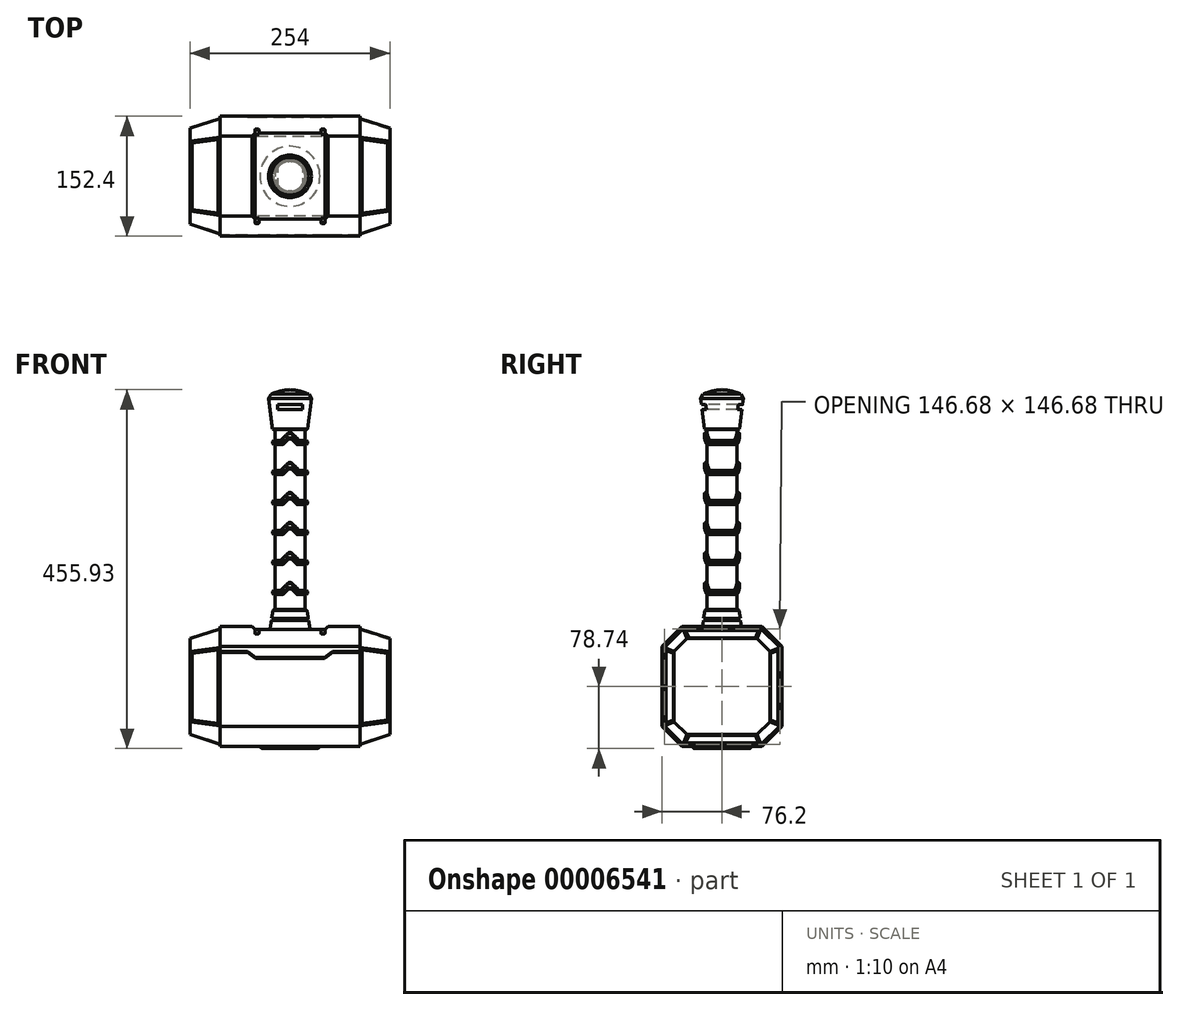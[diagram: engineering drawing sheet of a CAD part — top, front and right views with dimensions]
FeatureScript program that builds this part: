
annotation { "Feature Type Name" : "Feature", "Feature Type Description" : "" }
export const myFeature = defineFeature(function(context is Context, id is Id, definition is map)
    precondition{}
    {
        {
            var Q0;
            Q0=qCreatedBy(makeId("Top.planeOp"),FACE);
            var sketch = newSketch(context, id + "F0", { "sketchPlane" : qUnion([Q0])});
            skLineSegment(sketch, "E0.bottom", {"start": v(-88.9, -76.2) * mm, "end": v(88.9, -76.2) * mm});
            skLineSegment(sketch, "E0.top", {"start": v(-88.9, 76.2) * mm, "end": v(88.9, 76.2) * mm});
            skLineSegment(sketch, "E0.left", {"start": v(-88.9, -76.2) * mm, "end": v(-88.9, 76.2) * mm});
            skLineSegment(sketch, "E0.right", {"start": v(88.9, -76.2) * mm, "end": v(88.9, 76.2) * mm});
            skSolve(sketch);
        }
        {
            var Q0;
            Q0=makeQuery(id+"F0.imprint","IMPRINT",FACE,{"disambiguationData":[TD([[makeQuery(id+"F0.imprint","IMPRINT",EDGE,{"derivedFrom":sQuery(id+"F0.wireOp",EDGE,"E0.bottom")}),1.0]])]});
            extrude(context, id + "F1", {"entities" : qUnion([Q0]), "depth" : 152.4 * mm});
        }
        {
            var Q0;
            Q0=makeQuery(id+"F1.opExtrude","CAP_EDGE",EDGE,{"disambiguationData":[OSD([sQuery(id+"F0.wireOp",EDGE,"E0.bottom")])],"isStart":false});
            var Q1;
            Q1=makeQuery(id+"F1.opExtrude","CAP_EDGE",EDGE,{"disambiguationData":[OSD([sQuery(id+"F0.wireOp",EDGE,"E0.top")])],"isStart":false});
            var Q2;
            Q2=makeQuery(id+"F1.opExtrude","CAP_EDGE",EDGE,{"disambiguationData":[OSD([sQuery(id+"F0.wireOp",EDGE,"E0.bottom")])],"isStart":true});
            var Q3;
            Q3=makeQuery(id+"F1.opExtrude","CAP_EDGE",EDGE,{"disambiguationData":[OSD([sQuery(id+"F0.wireOp",EDGE,"E0.top")])],"isStart":true});
            chamfer(context, id + "F2", {"entities" : qUnion([Q0, Q1, Q2, Q3]), "width" : 25.4 * mm, "tangentPropagation" : true});
        }
        {
            var Q0;
            Q0=makeQuery(id+"F1.opExtrude","SWEPT_FACE",FACE,{"disambiguationData":[OSD([sQuery(id+"F0.wireOp",EDGE,"E0.left")])]});
            var sketch = newSketch(context, id + "F3", { "sketchPlane" : qUnion([Q0])});
            skLineSegment(sketch, "E1.0", {"start": v(-49.75, 149.86) * mm, "end": v(-73.66, 125.95) * mm});
            skLineSegment(sketch, "E1.1", {"start": v(49.75, 149.86) * mm, "end": v(-49.75, 149.86) * mm});
            skLineSegment(sketch, "E1.2", {"start": v(73.66, 125.95) * mm, "end": v(49.75, 149.86) * mm});
            skLineSegment(sketch, "E1.3", {"start": v(73.66, 26.45) * mm, "end": v(73.66, 125.95) * mm});
            skLineSegment(sketch, "E1.4", {"start": v(49.75, 2.54) * mm, "end": v(73.66, 26.45) * mm});
            skLineSegment(sketch, "E1.5", {"start": v(-73.66, 125.95) * mm, "end": v(-73.66, 26.45) * mm});
            skLineSegment(sketch, "E1.6", {"start": v(-49.75, 2.54) * mm, "end": v(49.75, 2.54) * mm});
            skLineSegment(sketch, "E1.7", {"start": v(-73.66, 26.45) * mm, "end": v(-49.75, 2.54) * mm});
            skSolve(sketch);
        }
        {
            var Q0;
            Q0=makeQuery(id+"F3.imprint","IMPRINT",FACE,{"disambiguationData":[TD([[makeQuery(id+"F3.imprint","IMPRINT",EDGE,{"derivedFrom":sQuery(id+"F3.wireOp",EDGE,"E1.0")}),1.0]])]});
            extrude(context, id + "F4", {"entities" : qUnion([Q0]), "operationType" : NewBodyOperationType.ADD, "depth" : 38.1 * mm});
        }
        {
            var Q0;
            Q0=makeQuery(id+"F4.opExtrude","CAP_FACE",FACE,{"disambiguationData":[OSD([sQuery(id+"F3.wireOp",EDGE,"E1.0"),sQuery(id+"F3.wireOp",EDGE,"E1.1"),sQuery(id+"F3.wireOp",EDGE,"E1.2"),sQuery(id+"F3.wireOp",EDGE,"E1.3"),sQuery(id+"F3.wireOp",EDGE,"E1.4"),sQuery(id+"F3.wireOp",EDGE,"E1.5"),sQuery(id+"F3.wireOp",EDGE,"E1.6"),sQuery(id+"F3.wireOp",EDGE,"E1.7")])],"isStart":false});
            chamfer(context, id + "F5", {"entities" : qUnion([Q0]), "chamferType" : ChamferType.OFFSET_ANGLE, "width" : 12.7 * mm, "oppositeDirection" : false, "angle" : 72 * degree, "tangentPropagation" : true});
        }
        {
            var Q0;
            Q0=makeQuery(id+"F1.opExtrude","SWEPT_FACE",FACE,{"disambiguationData":[OSD([sQuery(id+"F0.wireOp",EDGE,"E0.right")])]});
            var sketch = newSketch(context, id + "F6", { "sketchPlane" : qUnion([Q0])});
            skLineSegment(sketch, "E2.0", {"start": v(-73.66, 26.45) * mm, "end": v(-49.75, 2.54) * mm});
            skLineSegment(sketch, "E2.1", {"start": v(-73.66, 125.95) * mm, "end": v(-73.66, 26.45) * mm});
            skLineSegment(sketch, "E2.2", {"start": v(-49.75, 149.86) * mm, "end": v(-73.66, 125.95) * mm});
            skLineSegment(sketch, "E2.3", {"start": v(49.75, 149.86) * mm, "end": v(-49.75, 149.86) * mm});
            skLineSegment(sketch, "E2.4", {"start": v(73.66, 125.95) * mm, "end": v(49.75, 149.86) * mm});
            skLineSegment(sketch, "E2.5", {"start": v(-49.75, 2.54) * mm, "end": v(49.75, 2.54) * mm});
            skLineSegment(sketch, "E2.6", {"start": v(73.66, 26.45) * mm, "end": v(73.66, 125.95) * mm});
            skLineSegment(sketch, "E2.7", {"start": v(49.75, 2.54) * mm, "end": v(73.66, 26.45) * mm});
            skSolve(sketch);
        }
        {
            var Q0;
            Q0=makeQuery(id+"F6.imprint","IMPRINT",FACE,{"disambiguationData":[TD([[makeQuery(id+"F6.imprint","IMPRINT",EDGE,{"derivedFrom":sQuery(id+"F6.wireOp",EDGE,"E2.0")}),1.0]])]});
            extrude(context, id + "F7", {"entities" : qUnion([Q0]), "operationType" : NewBodyOperationType.ADD, "depth" : 38.1 * mm});
        }
        {
            var Q0;
            Q0=makeQuery(id+"F7.opExtrude","CAP_FACE",FACE,{"disambiguationData":[OSD([sQuery(id+"F6.wireOp",EDGE,"E2.0"),sQuery(id+"F6.wireOp",EDGE,"E2.1"),sQuery(id+"F6.wireOp",EDGE,"E2.2"),sQuery(id+"F6.wireOp",EDGE,"E2.3"),sQuery(id+"F6.wireOp",EDGE,"E2.4"),sQuery(id+"F6.wireOp",EDGE,"E2.5"),sQuery(id+"F6.wireOp",EDGE,"E2.6"),sQuery(id+"F6.wireOp",EDGE,"E2.7")])],"isStart":false});
            chamfer(context, id + "F8", {"entities" : qUnion([Q0]), "chamferType" : ChamferType.OFFSET_ANGLE, "width" : 12.7 * mm, "oppositeDirection" : false, "angle" : 72 * degree, "tangentPropagation" : true});
        }
        {
            var Q0;
            Q0=makeQuery(id+"F1.opExtrude","CAP_FACE",FACE,{"disambiguationData":[OSD([sQuery(id+"F0.wireOp",EDGE,"E0.bottom"),sQuery(id+"F0.wireOp",EDGE,"E0.top"),sQuery(id+"F0.wireOp",EDGE,"E0.left"),sQuery(id+"F0.wireOp",EDGE,"E0.right")])],"isStart":true});
            var sketch = newSketch(context, id + "F9", { "sketchPlane" : qUnion([Q0])});
            skCircle(sketch, "E3", {"center": v(0, 0) * mm, "radius": 38.1 * mm});
            skSolve(sketch);
        }
        {
            var Q0;
            Q0=makeQuery(id+"F9.imprint","IMPRINT",FACE,{"disambiguationData":[TD([[makeQuery(id+"F9.imprint","IMPRINT",EDGE,{"derivedFrom":sQuery(id+"F9.wireOp",EDGE,"E3")}),1.0]])]});
            extrude(context, id + "F10", {"entities" : qUnion([Q0]), "operationType" : NewBodyOperationType.ADD, "depth" : 2.54 * mm});
        }
        {
            var Q0;
            Q0=makeQuery(id+"F10.opExtrude","CAP_EDGE",EDGE,{"disambiguationData":[OSD([sQuery(id+"F9.wireOp",EDGE,"E3")])],"isStart":false});
            fillet(context, id + "F11", {"entities" : qUnion([Q0]), "radius" : 5.08 * mm, "tangentPropagation" : true, "allowEdgeOverflow" : false});
        }
        {
            var Q0;
            Q0=makeQuery(id+"F1.opExtrude","SWEPT_FACE",FACE,{"disambiguationData":[OSD([sQuery(id+"F0.wireOp",EDGE,"E0.bottom")])]});
            var sketch = newSketch(context, id + "F12", { "sketchPlane" : qUnion([Q0])});
            skLineSegment(sketch, "E4", {"start": v(0, 148.6) * mm, "end": v(44.45, 148.6) * mm});
            skLineSegment(sketch, "E5", {"start": v(44.45, 148.6) * mm, "end": v(51.87, 155.65) * mm});
            skLineSegment(sketch, "E6.0.MirrorCS", {"start": v(0, 148.6) * mm, "end": v(-44.45, 148.6) * mm});
            skLineSegment(sketch, "E7.0.MirrorCS", {"start": v(-44.45, 148.6) * mm, "end": v(-51.87, 155.65) * mm});
            skLineSegment(sketch, "E8", {"start": v(-51.87, 155.65) * mm, "end": v(51.87, 155.65) * mm});
            skSolve(sketch);
        }
        {
            var Q0;
            Q0=makeQuery(id+"F12.imprint","IMPRINT",FACE,{"disambiguationData":[TD([[makeQuery(id+"F12.imprint","IMPRINT",EDGE,{"derivedFrom":sQuery(id+"F12.wireOp",EDGE,"E4")}),1.0]])]});
            extrude(context, id + "F13", {"entities" : qUnion([Q0]), "operationType" : NewBodyOperationType.REMOVE, "oppositeDirection" : true, "depth" : 152.4 * mm});
        }
        {
            var Q0;
            {var subQ0=sQuery(id+"F0.wireOp",EDGE,"E0.top");Q0=makeQuery(id+"F2.opChamfer","BLEND_FACE",FACE,{"disambiguationData":[OSD([subQ0]),TDD([makeQuery(id+"F1.opExtrude","CAP_EDGE",EDGE,{"disambiguationData":[OSD([subQ0])],"isStart":false})])]});}
            var sketch = newSketch(context, id + "F14", { "sketchPlane" : qUnion([Q0])});
            skLineSegment(sketch, "E9.bottom", {"start": v(-44.45, 66.45) * mm, "end": v(-39.37, 66.45) * mm});
            skLineSegment(sketch, "E9.top", {"start": v(-43.18, 58.83) * mm, "end": v(-40.64, 58.83) * mm});
            skLineSegment(sketch, "E9.left", {"start": v(-44.45, 66.45) * mm, "end": v(-44.45, 60.1) * mm});
            skLineSegment(sketch, "E9.right", {"start": v(-39.37, 66.45) * mm, "end": v(-39.37, 60.1) * mm});
            skLineSegment(sketch, "E10.bottom", {"start": v(44.45, 66.45) * mm, "end": v(39.37, 66.45) * mm});
            skLineSegment(sketch, "E10.top", {"start": v(43.18, 58.83) * mm, "end": v(40.64, 58.83) * mm});
            skLineSegment(sketch, "E10.left", {"start": v(44.45, 66.45) * mm, "end": v(44.45, 60.1) * mm});
            skLineSegment(sketch, "E10.right", {"start": v(39.37, 66.45) * mm, "end": v(39.37, 60.1) * mm});
            skPoint(sketch, "E11.visualSharp", {"position": v(-44.45, 58.83) * mm});
            skArc(sketch, "E11.filletArc", {"start": v(-44.45, 60.1) * mm, "mid": v(-44.08, 59.2) * mm, "end": v(-43.18, 58.83) * mm});
            skPoint(sketch, "E12.visualSharp", {"position": v(-39.37, 58.83) * mm});
            skArc(sketch, "E12.filletArc", {"start": v(-40.64, 58.83) * mm, "mid": v(-39.74, 59.2) * mm, "end": v(-39.37, 60.1) * mm});
            skPoint(sketch, "E13.visualSharp", {"position": v(39.37, 58.83) * mm});
            skArc(sketch, "E13.filletArc", {"start": v(39.37, 60.1) * mm, "mid": v(39.74, 59.2) * mm, "end": v(40.64, 58.83) * mm});
            skPoint(sketch, "E14.visualSharp", {"position": v(44.45, 58.83) * mm});
            skArc(sketch, "E14.filletArc", {"start": v(43.18, 58.83) * mm, "mid": v(44.08, 59.2) * mm, "end": v(44.45, 60.1) * mm});
            skLineSegment(sketch, "E15.top", {"start": v(-44.45, 69.9) * mm, "end": v(-39.37, 69.9) * mm});
            skLineSegment(sketch, "E15.left", {"start": v(-44.45, 66.45) * mm, "end": v(-44.45, 69.9) * mm});
            skLineSegment(sketch, "E15.right", {"start": v(-39.37, 66.45) * mm, "end": v(-39.37, 69.9) * mm});
            skLineSegment(sketch, "E16.top", {"start": v(44.45, 69.9) * mm, "end": v(39.37, 69.9) * mm});
            skLineSegment(sketch, "E16.left", {"start": v(44.45, 66.45) * mm, "end": v(44.45, 69.9) * mm});
            skLineSegment(sketch, "E16.right", {"start": v(39.37, 66.45) * mm, "end": v(39.37, 69.9) * mm});
            skSolve(sketch);
        }
        {
            var Q0;
            Q0=makeQuery(id+"F14.imprint","IMPRINT",FACE,{"disambiguationData":[TD([[makeQuery(id+"F14.imprint","IMPRINT",EDGE,{"derivedFrom":sQuery(id+"F14.wireOp",EDGE,"E9.top")}),1.0]])]});
            var Q1;
            Q1=makeQuery(id+"F14.imprint","IMPRINT",FACE,{"disambiguationData":[TD([[makeQuery(id+"F14.imprint","IMPRINT",EDGE,{"derivedFrom":sQuery(id+"F14.wireOp",EDGE,"E9.bottom")}),-1.0]])]});
            var Q2;
            Q2=makeQuery(id+"F14.imprint","IMPRINT",FACE,{"disambiguationData":[TD([[makeQuery(id+"F14.imprint","IMPRINT",EDGE,{"derivedFrom":sQuery(id+"F14.wireOp",EDGE,"E10.top")}),-1.0]])]});
            var Q3;
            Q3=makeQuery(id+"F14.imprint","IMPRINT",FACE,{"disambiguationData":[TD([[makeQuery(id+"F14.imprint","IMPRINT",EDGE,{"derivedFrom":sQuery(id+"F14.wireOp",EDGE,"E10.bottom")}),-1.0]])]});
            extrude(context, id + "F15", {"entities" : qUnion([Q0, Q1, Q2, Q3]), "operationType" : NewBodyOperationType.REMOVE, "oppositeDirection" : true, "depth" : 1.27 * mm});
        }
        {
            var Q0;
            {var subQ0=sQuery(id+"F0.wireOp",EDGE,"E0.bottom");Q0=makeQuery(id+"F2.opChamfer","BLEND_FACE",FACE,{"disambiguationData":[OSD([subQ0]),TDD([makeQuery(id+"F1.opExtrude","CAP_EDGE",EDGE,{"disambiguationData":[OSD([subQ0])],"isStart":false})])]});}
            var sketch = newSketch(context, id + "F16", { "sketchPlane" : qUnion([Q0])});
            skLineSegment(sketch, "E17.bottom", {"start": v(-44.45, 66.45) * mm, "end": v(-39.37, 66.45) * mm});
            skLineSegment(sketch, "E17.top", {"start": v(-43.18, 58.83) * mm, "end": v(-40.64, 58.83) * mm});
            skLineSegment(sketch, "E17.left", {"start": v(-44.45, 66.45) * mm, "end": v(-44.45, 60.1) * mm});
            skLineSegment(sketch, "E17.right", {"start": v(-39.37, 66.45) * mm, "end": v(-39.37, 60.1) * mm});
            skLineSegment(sketch, "E18.bottom", {"start": v(44.45, 66.45) * mm, "end": v(39.37, 66.45) * mm});
            skLineSegment(sketch, "E18.top", {"start": v(43.18, 58.83) * mm, "end": v(40.64, 58.83) * mm});
            skLineSegment(sketch, "E18.left", {"start": v(44.45, 66.45) * mm, "end": v(44.45, 60.1) * mm});
            skLineSegment(sketch, "E18.right", {"start": v(39.37, 66.45) * mm, "end": v(39.37, 60.1) * mm});
            skPoint(sketch, "E19.visualSharp", {"position": v(-44.45, 58.83) * mm});
            skArc(sketch, "E19.filletArc", {"start": v(-44.45, 60.1) * mm, "mid": v(-44.08, 59.2) * mm, "end": v(-43.18, 58.83) * mm});
            skPoint(sketch, "E20.visualSharp", {"position": v(-39.37, 58.83) * mm});
            skArc(sketch, "E20.filletArc", {"start": v(-40.64, 58.83) * mm, "mid": v(-39.74, 59.2) * mm, "end": v(-39.37, 60.1) * mm});
            skPoint(sketch, "E21.visualSharp", {"position": v(39.37, 58.83) * mm});
            skArc(sketch, "E21.filletArc", {"start": v(39.37, 60.1) * mm, "mid": v(39.74, 59.2) * mm, "end": v(40.64, 58.83) * mm});
            skPoint(sketch, "E22.visualSharp", {"position": v(44.45, 58.83) * mm});
            skArc(sketch, "E22.filletArc", {"start": v(43.18, 58.83) * mm, "mid": v(44.08, 59.2) * mm, "end": v(44.45, 60.1) * mm});
            skLineSegment(sketch, "E23.top", {"start": v(-44.45, 70.2) * mm, "end": v(-39.37, 70.2) * mm});
            skLineSegment(sketch, "E23.left", {"start": v(-44.45, 66.45) * mm, "end": v(-44.45, 70.2) * mm});
            skLineSegment(sketch, "E23.right", {"start": v(-39.37, 66.45) * mm, "end": v(-39.37, 70.2) * mm});
            skLineSegment(sketch, "E24.top", {"start": v(44.45, 71) * mm, "end": v(39.37, 71) * mm});
            skLineSegment(sketch, "E24.left", {"start": v(44.45, 66.45) * mm, "end": v(44.45, 71) * mm});
            skLineSegment(sketch, "E24.right", {"start": v(39.37, 66.45) * mm, "end": v(39.37, 71) * mm});
            skSolve(sketch);
        }
        {
            var Q0;
            Q0=makeQuery(id+"F16.imprint","IMPRINT",FACE,{"disambiguationData":[TD([[makeQuery(id+"F16.imprint","IMPRINT",EDGE,{"derivedFrom":sQuery(id+"F16.wireOp",EDGE,"E17.top")}),1.0]])]});
            var Q1;
            Q1=makeQuery(id+"F16.imprint","IMPRINT",FACE,{"disambiguationData":[TD([[makeQuery(id+"F16.imprint","IMPRINT",EDGE,{"derivedFrom":sQuery(id+"F16.wireOp",EDGE,"E17.bottom")}),-1.0]])]});
            var Q2;
            Q2=makeQuery(id+"F16.imprint","IMPRINT",FACE,{"disambiguationData":[TD([[makeQuery(id+"F16.imprint","IMPRINT",EDGE,{"derivedFrom":sQuery(id+"F16.wireOp",EDGE,"E18.top")}),-1.0]])]});
            var Q3;
            Q3=makeQuery(id+"F16.imprint","IMPRINT",FACE,{"disambiguationData":[TD([[makeQuery(id+"F16.imprint","IMPRINT",EDGE,{"derivedFrom":sQuery(id+"F16.wireOp",EDGE,"E18.bottom")}),-1.0]])]});
            extrude(context, id + "F17", {"entities" : qUnion([Q0, Q1, Q2, Q3]), "operationType" : NewBodyOperationType.REMOVE, "oppositeDirection" : true, "depth" : 1.27 * mm});
        }
        {
            var Q0;
            Q0=makeQuery(id+"F1.opExtrude","SWEPT_FACE",FACE,{"disambiguationData":[OSD([sQuery(id+"F0.wireOp",EDGE,"E0.bottom")])]});
            var sketch = newSketch(context, id + "F18", { "sketchPlane" : qUnion([Q0])});
            skLineSegment(sketch, "E25", {"start": v(88.9, 120.65) * mm, "end": v(53.9, 120.65) * mm});
            skLineSegment(sketch, "E26", {"start": v(0, 113.03) * mm, "end": v(43.78, 113.03) * mm});
            skLineSegment(sketch, "E27", {"start": v(43.78, 113.03) * mm, "end": v(53.9, 120.65) * mm});
            skLineSegment(sketch, "E28.0.MirrorCS", {"start": v(0, 113.03) * mm, "end": v(-43.78, 113.03) * mm});
            skLineSegment(sketch, "E29.0.MirrorCS", {"start": v(-43.78, 113.03) * mm, "end": v(-53.9, 120.65) * mm});
            skLineSegment(sketch, "E30.trimOffspring", {"start": v(-53.9, 120.65) * mm, "end": v(-88.9, 120.65) * mm});
            skPoint(sketch, "E31.orphan", {"position": v(0, 120.65) * mm});
            skLineSegment(sketch, "E32.0", {"start": v(0, 111.76) * mm, "end": v(43.78, 111.76) * mm});
            skLineSegment(sketch, "E32.1", {"start": v(0, 111.76) * mm, "end": v(-43.78, 111.76) * mm});
            skLineSegment(sketch, "E33.0", {"start": v(88.9, 119.38) * mm, "end": v(53.94, 119.38) * mm});
            skLineSegment(sketch, "E34.0", {"start": v(-53.9, 119.38) * mm, "end": v(-88.9, 119.38) * mm});
            skLineSegment(sketch, "E35", {"start": v(-53.9, 119.38) * mm, "end": v(-43.78, 111.76) * mm});
            skLineSegment(sketch, "E36", {"start": v(53.94, 119.38) * mm, "end": v(43.78, 111.76) * mm});
            skSolve(sketch);
        }
        {
            var Q0;
            Q0=makeQuery(id+"F1.opExtrude","SWEPT_FACE",FACE,{"disambiguationData":[OSD([sQuery(id+"F0.wireOp",EDGE,"E0.top")])]});
            var sketch = newSketch(context, id + "F19", { "sketchPlane" : qUnion([Q0])});
            skLineSegment(sketch, "E37.0", {"start": v(0, 111.76) * mm, "end": v(43.78, 111.76) * mm});
            skLineSegment(sketch, "E38.0", {"start": v(0, 113.03) * mm, "end": v(-43.78, 113.03) * mm});
            skLineSegment(sketch, "E39.0", {"start": v(0, 111.76) * mm, "end": v(-43.78, 111.76) * mm});
            skLineSegment(sketch, "E40.0", {"start": v(-53.94, 119.38) * mm, "end": v(-43.78, 111.76) * mm});
            skLineSegment(sketch, "E40.1", {"start": v(-43.78, 113.03) * mm, "end": v(-53.9, 120.65) * mm});
            skLineSegment(sketch, "E41.0", {"start": v(-88.9, 119.38) * mm, "end": v(-53.94, 119.38) * mm});
            skLineSegment(sketch, "E41.1", {"start": v(-88.9, 120.65) * mm, "end": v(-53.9, 120.65) * mm});
            skLineSegment(sketch, "E42.0", {"start": v(53.9, 119.38) * mm, "end": v(88.9, 119.38) * mm});
            skLineSegment(sketch, "E42.1", {"start": v(53.9, 120.65) * mm, "end": v(88.9, 120.65) * mm});
            skLineSegment(sketch, "E43.0", {"start": v(53.9, 119.38) * mm, "end": v(43.78, 111.76) * mm});
            skLineSegment(sketch, "E43.1", {"start": v(43.78, 113.03) * mm, "end": v(53.9, 120.65) * mm});
            skLineSegment(sketch, "E43.2", {"start": v(0, 113.03) * mm, "end": v(43.78, 113.03) * mm});
            skSolve(sketch);
        }
        {
            var Q0;
            Q0=makeQuery(id+"F19.imprint","IMPRINT",FACE,{"disambiguationData":[TD([[makeQuery(id+"F19.imprint","IMPRINT",EDGE,{"derivedFrom":sQuery(id+"F19.wireOp",EDGE,"E37.0")}),1.0]])]});
            extrude(context, id + "F20", {"entities" : qUnion([Q0]), "operationType" : NewBodyOperationType.REMOVE, "oppositeDirection" : true, "depth" : 1.27 * mm});
        }
        {
            var Q0;
            {var subQ6=sQuery(id+"F18.wireOp",EDGE,"E25");Q0=makeQuery(id+"F18.imprint","IMPRINT",FACE,{"disambiguationData":[TD([[makeQuery(id+"F18.imprint","IMPRINT",EDGE,{"derivedFrom":subQ6}),1.0]])]});}
            extrude(context, id + "F21", {"entities" : qUnion([Q0]), "operationType" : NewBodyOperationType.REMOVE, "oppositeDirection" : true, "depth" : 1.27 * mm});
        }
        {
            var Q0;
            Q0=makeQuery(id+"F8.opChamfer","BLEND_FACE",FACE,{"disambiguationData":[OSD([sQuery(id+"F6.wireOp",EDGE,"E2.3")])]});
            var sketch = newSketch(context, id + "F22", { "sketchPlane" : qUnion([Q0])});
            skLineSegment(sketch, "E44.0", {"start": v(40.88, -46.73) * mm, "end": v(75.86, -42.25) * mm});
            skLineSegment(sketch, "E44.1", {"start": v(40.88, 46.73) * mm, "end": v(40.88, -46.73) * mm});
            skLineSegment(sketch, "E44.2", {"start": v(40.88, 46.73) * mm, "end": v(75.86, 42.25) * mm});
            skLineSegment(sketch, "E44.3", {"start": v(75.86, -42.25) * mm, "end": v(75.86, 42.25) * mm});
            skSolve(sketch);
        }
        {
            var Q0;
            Q0=makeQuery(id+"F22.imprint","IMPRINT",FACE,{"disambiguationData":[TD([[makeQuery(id+"F22.imprint","IMPRINT",EDGE,{"derivedFrom":sQuery(id+"F22.wireOp",EDGE,"E44.0")}),1.0]])]});
            extrude(context, id + "F23", {"entities" : qUnion([Q0]), "operationType" : NewBodyOperationType.REMOVE, "oppositeDirection" : true, "depth" : 1.27 * mm});
        }
        {
            var Q0;
            Q0=qCreatedBy(makeId("Front.planeOp"),FACE);
            var sketch = newSketch(context, id + "F24", { "sketchPlane" : qUnion([Q0])});
            skLineSegment(sketch, "E45", {"start": v(0, 76.2) * mm, "end": v(-188.8, 76.2) * mm});
            skSolve(sketch);
        }
        {
            var Q0;
            Q0=makeQuery(id+"F23.boolean.opBoolean","COPY",FACE,{"derivedFrom":makeQuery(id+"F23.opExtrude","CAP_FACE",FACE,{"disambiguationData":[OSD([sQuery(id+"F22.wireOp",EDGE,"E44.0"),sQuery(id+"F22.wireOp",EDGE,"E44.1"),sQuery(id+"F22.wireOp",EDGE,"E44.2"),sQuery(id+"F22.wireOp",EDGE,"E44.3")])],"isStart":false})});
            var Q1;
            Q1=makeQuery(id+"F23.boolean.opBoolean","COPY",FACE,{"derivedFrom":makeQuery(id+"F23.opExtrude","SWEPT_FACE",FACE,{"disambiguationData":[OSD([sQuery(id+"F22.wireOp",EDGE,"E44.3")])]})});
            var Q2;
            Q2=makeQuery(id+"F23.boolean.opBoolean","COPY",FACE,{"derivedFrom":makeQuery(id+"F23.opExtrude","SWEPT_FACE",FACE,{"disambiguationData":[OSD([sQuery(id+"F22.wireOp",EDGE,"E44.0")])]})});
            var Q3;
            Q3=makeQuery(id+"F23.boolean.opBoolean","COPY",FACE,{"derivedFrom":makeQuery(id+"F23.opExtrude","SWEPT_FACE",FACE,{"disambiguationData":[OSD([sQuery(id+"F22.wireOp",EDGE,"E44.1")])]})});
            var Q4;
            Q4=makeQuery(id+"F23.boolean.opBoolean","COPY",FACE,{"derivedFrom":makeQuery(id+"F23.opExtrude","SWEPT_FACE",FACE,{"disambiguationData":[OSD([sQuery(id+"F22.wireOp",EDGE,"E44.2")])]})});
            var Q5;
            Q5=sQuery(id+"F24.wireOp",EDGE,"E45");
            circularPattern(context, id + "F25", {"faces" : qUnion([Q0, Q1, Q2, Q3, Q4]), "axis" : qUnion([Q5]), "angle" : 90 * degree, "instanceCount" : round(4), "patternType" : PatternType.FACE});
        }
        {
            var Q0;
            Q0=makeQuery(id+"F5.opChamfer","BLEND_FACE",FACE,{"disambiguationData":[OSD([sQuery(id+"F3.wireOp",EDGE,"E1.6")])]});
            var sketch = newSketch(context, id + "F26", { "sketchPlane" : qUnion([Q0])});
            skLineSegment(sketch, "E46.0", {"start": v(-87.97, 46.73) * mm, "end": v(-122.95, 42.25) * mm});
            skLineSegment(sketch, "E46.1", {"start": v(-87.97, -46.73) * mm, "end": v(-87.97, 46.73) * mm});
            skLineSegment(sketch, "E46.2", {"start": v(-87.97, -46.73) * mm, "end": v(-122.95, -42.25) * mm});
            skLineSegment(sketch, "E46.3", {"start": v(-122.95, 42.25) * mm, "end": v(-122.95, -42.25) * mm});
            skSolve(sketch);
        }
        {
            var Q0;
            Q0=makeQuery(id+"F26.imprint","IMPRINT",FACE,{"disambiguationData":[TD([[makeQuery(id+"F26.imprint","IMPRINT",EDGE,{"derivedFrom":sQuery(id+"F26.wireOp",EDGE,"E46.0")}),1.0]])]});
            extrude(context, id + "F27", {"entities" : qUnion([Q0]), "operationType" : NewBodyOperationType.REMOVE, "oppositeDirection" : true, "depth" : 1.27 * mm});
        }
        {
            var Q0;
            Q0=qCreatedBy(makeId("Front.planeOp"),FACE);
            var sketch = newSketch(context, id + "F28", { "sketchPlane" : qUnion([Q0])});
            skLineSegment(sketch, "E47", {"start": v(0, 76.2) * mm, "end": v(-234.44, 76.2) * mm});
            skSolve(sketch);
        }
        {
            var Q0;
            Q0=makeQuery(id+"F27.boolean.opBoolean","COPY",FACE,{"derivedFrom":makeQuery(id+"F27.opExtrude","CAP_FACE",FACE,{"disambiguationData":[OSD([sQuery(id+"F26.wireOp",EDGE,"E46.0"),sQuery(id+"F26.wireOp",EDGE,"E46.1"),sQuery(id+"F26.wireOp",EDGE,"E46.2"),sQuery(id+"F26.wireOp",EDGE,"E46.3")])],"isStart":false})});
            var Q1;
            Q1=makeQuery(id+"F27.boolean.opBoolean","COPY",FACE,{"derivedFrom":makeQuery(id+"F27.opExtrude","SWEPT_FACE",FACE,{"disambiguationData":[OSD([sQuery(id+"F26.wireOp",EDGE,"E46.2")])]})});
            var Q2;
            Q2=makeQuery(id+"F27.boolean.opBoolean","COPY",FACE,{"derivedFrom":makeQuery(id+"F27.opExtrude","SWEPT_FACE",FACE,{"disambiguationData":[OSD([sQuery(id+"F26.wireOp",EDGE,"E46.3")])]})});
            var Q3;
            Q3=makeQuery(id+"F27.boolean.opBoolean","COPY",FACE,{"derivedFrom":makeQuery(id+"F27.opExtrude","SWEPT_FACE",FACE,{"disambiguationData":[OSD([sQuery(id+"F26.wireOp",EDGE,"E46.0")])]})});
            var Q4;
            Q4=makeQuery(id+"F27.boolean.opBoolean","COPY",FACE,{"derivedFrom":makeQuery(id+"F27.opExtrude","SWEPT_FACE",FACE,{"disambiguationData":[OSD([sQuery(id+"F26.wireOp",EDGE,"E46.1")])]})});
            var Q5;
            Q5=sQuery(id+"F28.wireOp",EDGE,"E47");
            circularPattern(context, id + "F29", {"faces" : qUnion([Q0, Q1, Q2, Q3, Q4]), "axis" : qUnion([Q5]), "angle" : 90 * degree, "instanceCount" : round(4), "patternType" : PatternType.FACE});
        }
        {
            var Q0;
            Q0=makeQuery(id+"F13.boolean.opBoolean","COPY",FACE,{"derivedFrom":makeQuery(id+"F13.opExtrude","SWEPT_FACE",FACE,{"disambiguationData":[OSD([sQuery(id+"F12.wireOp",EDGE,"E4"),sQuery(id+"F12.wireOp",EDGE,"E6.0.MirrorCS")])]})});
            var sketch = newSketch(context, id + "F30", { "sketchPlane" : qUnion([Q0])});
            skCircle(sketch, "E48", {"center": v(0, 0) * mm, "radius": 25.4 * mm});
            skSolve(sketch);
        }
        {
            var Q0;
            Q0=makeQuery(id+"F30.imprint","IMPRINT",FACE,{"disambiguationData":[TD([[makeQuery(id+"F30.imprint","IMPRINT",EDGE,{"derivedFrom":sQuery(id+"F30.wireOp",EDGE,"E48")}),1.0]])]});
            extrude(context, id + "F31", {"entities" : qUnion([Q0]), "operationType" : NewBodyOperationType.ADD, "depth" : 25.4 * mm});
        }
        {
            var Q0;
            Q0=makeQuery(id+"F31.opExtrude","CAP_FACE",FACE,{"disambiguationData":[OSD([sQuery(id+"F30.wireOp",EDGE,"E48")])],"isStart":false});
            var sketch = newSketch(context, id + "F32", { "sketchPlane" : qUnion([Q0])});
            skCircle(sketch, "E49", {"center": v(0, 0) * mm, "radius": 19.05 * mm});
            skSolve(sketch);
        }
        {
            var Q0;
            Q0=makeQuery(id+"F32.imprint","IMPRINT",FACE,{"disambiguationData":[TD([[makeQuery(id+"F32.imprint","IMPRINT",EDGE,{"derivedFrom":sQuery(id+"F32.wireOp",EDGE,"E49")}),1.0]])]});
            extrude(context, id + "F33", {"entities" : qUnion([Q0]), "operationType" : NewBodyOperationType.ADD, "depth" : 228.6 * mm});
        }
        {
            var Q0;
            Q0=qCreatedBy(makeId("Front.planeOp"),FACE);
            var sketch = newSketch(context, id + "F34", { "sketchPlane" : qUnion([Q0])});
            skLineSegment(sketch, "E50", {"start": v(-61.39, 193.04) * mm, "end": v(-10.56, 193.04) * mm});
            skLineSegment(sketch, "E51", {"start": v(-61.56, 198.12) * mm, "end": v(-13.76, 198.12) * mm});
            skLineSegment(sketch, "E52", {"start": v(-61.56, 198.12) * mm, "end": v(-61.39, 193.04) * mm});
            skLineSegment(sketch, "E53", {"start": v(66.53, 198.12) * mm, "end": v(76.74, 193.04) * mm});
            skLineSegment(sketch, "E54", {"start": v(0, 0) * mm, "end": v(0, 558.05) * mm, "construction": true});
            skLineSegment(sketch, "E55", {"start": v(-7.86, 194.16) * mm, "end": v(-2.7, 199.33) * mm});
            skLineSegment(sketch, "E56", {"start": v(2.7, 199.33) * mm, "end": v(7.86, 194.16) * mm});
            skLineSegment(sketch, "E57.0", {"start": v(2.7, 207.61) * mm, "end": v(11.07, 199.24) * mm});
            skLineSegment(sketch, "E57.1", {"start": v(-11.07, 199.24) * mm, "end": v(-2.7, 207.61) * mm});
            skLineSegment(sketch, "E58.trimOffspring", {"start": v(10.56, 193.04) * mm, "end": v(76.74, 193.04) * mm});
            skLineSegment(sketch, "E59.trimOffspring", {"start": v(13.76, 198.12) * mm, "end": v(66.53, 198.12) * mm});
            skPoint(sketch, "E60.visualSharp", {"position": v(-8.98, 193.04) * mm});
            skArc(sketch, "E60.filletArc", {"start": v(-10.56, 193.04) * mm, "mid": v(-9.1, 193.33) * mm, "end": v(-7.86, 194.16) * mm});
            skPoint(sketch, "E61.visualSharp", {"position": v(-12.19, 198.12) * mm});
            skArc(sketch, "E61.filletArc", {"start": v(-13.76, 198.12) * mm, "mid": v(-12.3, 198.41) * mm, "end": v(-11.07, 199.24) * mm});
            skPoint(sketch, "E62.visualSharp", {"position": v(0, 202.02) * mm});
            skArc(sketch, "E62.filletArc", {"start": v(2.7, 199.33) * mm, "mid": v(0, 200.44) * mm, "end": v(-2.7, 199.33) * mm});
            skPoint(sketch, "E63.visualSharp", {"position": v(0, 210.3) * mm});
            skArc(sketch, "E63.filletArc", {"start": v(2.7, 207.61) * mm, "mid": v(0, 208.73) * mm, "end": v(-2.7, 207.61) * mm});
            skPoint(sketch, "E64.visualSharp", {"position": v(8.98, 193.04) * mm});
            skArc(sketch, "E64.filletArc", {"start": v(7.86, 194.16) * mm, "mid": v(9.1, 193.33) * mm, "end": v(10.56, 193.04) * mm});
            skPoint(sketch, "E65.visualSharp", {"position": v(12.19, 198.12) * mm});
            skArc(sketch, "E65.filletArc", {"start": v(11.07, 199.24) * mm, "mid": v(12.3, 198.41) * mm, "end": v(13.76, 198.12) * mm});
            skLineSegment(sketch, "E66.0.1.0", {"start": v(-61.56, 236.22) * mm, "end": v(-13.76, 236.22) * mm});
            skLineSegment(sketch, "E66.0.1.1", {"start": v(-11.07, 237.34) * mm, "end": v(-2.7, 245.71) * mm});
            skLineSegment(sketch, "E66.0.1.2", {"start": v(2.7, 245.71) * mm, "end": v(11.07, 237.34) * mm});
            skArc(sketch, "E66.0.1.3", {"start": v(2.7, 245.71) * mm, "mid": v(0, 246.83) * mm, "end": v(-2.7, 245.71) * mm});
            skArc(sketch, "E66.0.1.4", {"start": v(2.7, 237.43) * mm, "mid": v(0, 238.54) * mm, "end": v(-2.7, 237.43) * mm});
            skLineSegment(sketch, "E66.0.1.5", {"start": v(2.7, 237.43) * mm, "end": v(7.86, 232.26) * mm});
            skLineSegment(sketch, "E66.0.1.6", {"start": v(-7.86, 232.26) * mm, "end": v(-2.7, 237.43) * mm});
            skPoint(sketch, "E66.0.1.7", {"position": v(-8.98, 231.14) * mm});
            skArc(sketch, "E66.0.1.8", {"start": v(-10.56, 231.14) * mm, "mid": v(-9.1, 231.43) * mm, "end": v(-7.86, 232.26) * mm});
            skArc(sketch, "E66.0.1.9", {"start": v(-13.76, 236.22) * mm, "mid": v(-12.3, 236.51) * mm, "end": v(-11.07, 237.34) * mm});
            skArc(sketch, "E66.0.1.10", {"start": v(7.86, 232.26) * mm, "mid": v(9.1, 231.43) * mm, "end": v(10.56, 231.14) * mm});
            skArc(sketch, "E66.0.1.11", {"start": v(11.07, 237.34) * mm, "mid": v(12.3, 236.51) * mm, "end": v(13.76, 236.22) * mm});
            skLineSegment(sketch, "E66.0.1.12", {"start": v(10.56, 231.14) * mm, "end": v(76.74, 231.14) * mm});
            skLineSegment(sketch, "E66.0.1.13", {"start": v(13.76, 236.22) * mm, "end": v(66.53, 236.22) * mm});
            skLineSegment(sketch, "E66.0.1.14", {"start": v(66.53, 236.22) * mm, "end": v(76.74, 231.14) * mm});
            skLineSegment(sketch, "E66.0.1.15", {"start": v(-61.56, 236.22) * mm, "end": v(-61.39, 231.14) * mm});
            skLineSegment(sketch, "E66.0.1.16", {"start": v(-61.39, 231.14) * mm, "end": v(-10.56, 231.14) * mm});
            skLineSegment(sketch, "E66.0.2.0", {"start": v(-61.56, 274.32) * mm, "end": v(-13.76, 274.32) * mm});
            skLineSegment(sketch, "E66.0.2.1", {"start": v(-11.07, 275.44) * mm, "end": v(-2.7, 283.81) * mm});
            skLineSegment(sketch, "E66.0.2.2", {"start": v(2.7, 283.81) * mm, "end": v(11.07, 275.44) * mm});
            skArc(sketch, "E66.0.2.3", {"start": v(2.7, 283.81) * mm, "mid": v(0, 284.93) * mm, "end": v(-2.7, 283.81) * mm});
            skArc(sketch, "E66.0.2.4", {"start": v(2.7, 275.53) * mm, "mid": v(0, 276.64) * mm, "end": v(-2.7, 275.53) * mm});
            skLineSegment(sketch, "E66.0.2.5", {"start": v(2.7, 275.53) * mm, "end": v(7.86, 270.36) * mm});
            skLineSegment(sketch, "E66.0.2.6", {"start": v(-7.86, 270.36) * mm, "end": v(-2.7, 275.53) * mm});
            skPoint(sketch, "E66.0.2.7", {"position": v(-8.98, 269.24) * mm});
            skArc(sketch, "E66.0.2.8", {"start": v(-10.56, 269.24) * mm, "mid": v(-9.1, 269.53) * mm, "end": v(-7.86, 270.36) * mm});
            skArc(sketch, "E66.0.2.9", {"start": v(-13.76, 274.32) * mm, "mid": v(-12.3, 274.61) * mm, "end": v(-11.07, 275.44) * mm});
            skArc(sketch, "E66.0.2.10", {"start": v(7.86, 270.36) * mm, "mid": v(9.1, 269.53) * mm, "end": v(10.56, 269.24) * mm});
            skArc(sketch, "E66.0.2.11", {"start": v(11.07, 275.44) * mm, "mid": v(12.3, 274.61) * mm, "end": v(13.76, 274.32) * mm});
            skLineSegment(sketch, "E66.0.2.12", {"start": v(10.56, 269.24) * mm, "end": v(76.74, 269.24) * mm});
            skLineSegment(sketch, "E66.0.2.13", {"start": v(13.76, 274.32) * mm, "end": v(66.53, 274.32) * mm});
            skLineSegment(sketch, "E66.0.2.14", {"start": v(66.53, 274.32) * mm, "end": v(76.74, 269.24) * mm});
            skLineSegment(sketch, "E66.0.2.15", {"start": v(-61.56, 274.32) * mm, "end": v(-61.39, 269.24) * mm});
            skLineSegment(sketch, "E66.0.2.16", {"start": v(-61.39, 269.24) * mm, "end": v(-10.56, 269.24) * mm});
            skLineSegment(sketch, "E66.0.3.0", {"start": v(-61.56, 312.42) * mm, "end": v(-13.76, 312.42) * mm});
            skLineSegment(sketch, "E66.0.3.1", {"start": v(-11.07, 313.54) * mm, "end": v(-2.7, 321.91) * mm});
            skLineSegment(sketch, "E66.0.3.2", {"start": v(2.7, 321.91) * mm, "end": v(11.07, 313.54) * mm});
            skArc(sketch, "E66.0.3.3", {"start": v(2.7, 321.91) * mm, "mid": v(0, 323.03) * mm, "end": v(-2.7, 321.91) * mm});
            skArc(sketch, "E66.0.3.4", {"start": v(2.7, 313.63) * mm, "mid": v(0, 314.74) * mm, "end": v(-2.7, 313.63) * mm});
            skLineSegment(sketch, "E66.0.3.5", {"start": v(2.7, 313.63) * mm, "end": v(7.86, 308.46) * mm});
            skLineSegment(sketch, "E66.0.3.6", {"start": v(-7.86, 308.46) * mm, "end": v(-2.7, 313.63) * mm});
            skPoint(sketch, "E66.0.3.7", {"position": v(-8.98, 307.34) * mm});
            skArc(sketch, "E66.0.3.8", {"start": v(-10.56, 307.34) * mm, "mid": v(-9.1, 307.63) * mm, "end": v(-7.86, 308.46) * mm});
            skArc(sketch, "E66.0.3.9", {"start": v(-13.76, 312.42) * mm, "mid": v(-12.3, 312.71) * mm, "end": v(-11.07, 313.54) * mm});
            skArc(sketch, "E66.0.3.10", {"start": v(7.86, 308.46) * mm, "mid": v(9.1, 307.63) * mm, "end": v(10.56, 307.34) * mm});
            skArc(sketch, "E66.0.3.11", {"start": v(11.07, 313.54) * mm, "mid": v(12.3, 312.71) * mm, "end": v(13.76, 312.42) * mm});
            skLineSegment(sketch, "E66.0.3.12", {"start": v(10.56, 307.34) * mm, "end": v(76.74, 307.34) * mm});
            skLineSegment(sketch, "E66.0.3.13", {"start": v(13.76, 312.42) * mm, "end": v(66.53, 312.42) * mm});
            skLineSegment(sketch, "E66.0.3.14", {"start": v(66.53, 312.42) * mm, "end": v(76.74, 307.34) * mm});
            skLineSegment(sketch, "E66.0.3.15", {"start": v(-61.56, 312.42) * mm, "end": v(-61.39, 307.34) * mm});
            skLineSegment(sketch, "E66.0.3.16", {"start": v(-61.39, 307.34) * mm, "end": v(-10.56, 307.34) * mm});
            skLineSegment(sketch, "E66.0.4.0", {"start": v(-61.56, 350.52) * mm, "end": v(-13.76, 350.52) * mm});
            skLineSegment(sketch, "E66.0.4.1", {"start": v(-11.07, 351.64) * mm, "end": v(-2.7, 360.01) * mm});
            skLineSegment(sketch, "E66.0.4.2", {"start": v(2.7, 360.01) * mm, "end": v(11.07, 351.64) * mm});
            skArc(sketch, "E66.0.4.3", {"start": v(2.7, 360.01) * mm, "mid": v(0, 361.13) * mm, "end": v(-2.7, 360.01) * mm});
            skArc(sketch, "E66.0.4.4", {"start": v(2.7, 351.73) * mm, "mid": v(0, 352.84) * mm, "end": v(-2.7, 351.73) * mm});
            skLineSegment(sketch, "E66.0.4.5", {"start": v(2.7, 351.73) * mm, "end": v(7.86, 346.56) * mm});
            skLineSegment(sketch, "E66.0.4.6", {"start": v(-7.86, 346.56) * mm, "end": v(-2.7, 351.73) * mm});
            skPoint(sketch, "E66.0.4.7", {"position": v(-8.98, 345.44) * mm});
            skArc(sketch, "E66.0.4.8", {"start": v(-10.56, 345.44) * mm, "mid": v(-9.1, 345.73) * mm, "end": v(-7.86, 346.56) * mm});
            skArc(sketch, "E66.0.4.9", {"start": v(-13.76, 350.52) * mm, "mid": v(-12.3, 350.81) * mm, "end": v(-11.07, 351.64) * mm});
            skArc(sketch, "E66.0.4.10", {"start": v(7.86, 346.56) * mm, "mid": v(9.1, 345.73) * mm, "end": v(10.56, 345.44) * mm});
            skArc(sketch, "E66.0.4.11", {"start": v(11.07, 351.64) * mm, "mid": v(12.3, 350.81) * mm, "end": v(13.76, 350.52) * mm});
            skLineSegment(sketch, "E66.0.4.12", {"start": v(10.56, 345.44) * mm, "end": v(76.74, 345.44) * mm});
            skLineSegment(sketch, "E66.0.4.13", {"start": v(13.76, 350.52) * mm, "end": v(66.53, 350.52) * mm});
            skLineSegment(sketch, "E66.0.4.14", {"start": v(66.53, 350.52) * mm, "end": v(76.74, 345.44) * mm});
            skLineSegment(sketch, "E66.0.4.15", {"start": v(-61.56, 350.52) * mm, "end": v(-61.39, 345.44) * mm});
            skLineSegment(sketch, "E66.0.4.16", {"start": v(-61.39, 345.44) * mm, "end": v(-10.56, 345.44) * mm});
            skLineSegment(sketch, "E66.0.5.0", {"start": v(-61.56, 388.62) * mm, "end": v(-13.76, 388.62) * mm});
            skLineSegment(sketch, "E66.0.5.1", {"start": v(-11.07, 389.74) * mm, "end": v(-2.7, 398.11) * mm});
            skLineSegment(sketch, "E66.0.5.2", {"start": v(2.7, 398.11) * mm, "end": v(11.07, 389.74) * mm});
            skArc(sketch, "E66.0.5.3", {"start": v(2.7, 398.11) * mm, "mid": v(0, 399.23) * mm, "end": v(-2.7, 398.11) * mm});
            skArc(sketch, "E66.0.5.4", {"start": v(2.7, 389.83) * mm, "mid": v(0, 390.94) * mm, "end": v(-2.7, 389.83) * mm});
            skLineSegment(sketch, "E66.0.5.5", {"start": v(2.7, 389.83) * mm, "end": v(7.86, 384.66) * mm});
            skLineSegment(sketch, "E66.0.5.6", {"start": v(-7.86, 384.66) * mm, "end": v(-2.7, 389.83) * mm});
            skPoint(sketch, "E66.0.5.7", {"position": v(-8.98, 383.54) * mm});
            skArc(sketch, "E66.0.5.8", {"start": v(-10.56, 383.54) * mm, "mid": v(-9.1, 383.83) * mm, "end": v(-7.86, 384.66) * mm});
            skArc(sketch, "E66.0.5.9", {"start": v(-13.76, 388.62) * mm, "mid": v(-12.3, 388.91) * mm, "end": v(-11.07, 389.74) * mm});
            skArc(sketch, "E66.0.5.10", {"start": v(7.86, 384.66) * mm, "mid": v(9.1, 383.83) * mm, "end": v(10.56, 383.54) * mm});
            skArc(sketch, "E66.0.5.11", {"start": v(11.07, 389.74) * mm, "mid": v(12.3, 388.91) * mm, "end": v(13.76, 388.62) * mm});
            skLineSegment(sketch, "E66.0.5.12", {"start": v(10.56, 383.54) * mm, "end": v(76.74, 383.54) * mm});
            skLineSegment(sketch, "E66.0.5.13", {"start": v(13.76, 388.62) * mm, "end": v(66.53, 388.62) * mm});
            skLineSegment(sketch, "E66.0.5.14", {"start": v(66.53, 388.62) * mm, "end": v(76.74, 383.54) * mm});
            skLineSegment(sketch, "E66.0.5.15", {"start": v(-61.56, 388.62) * mm, "end": v(-61.39, 383.54) * mm});
            skLineSegment(sketch, "E66.0.5.16", {"start": v(-61.39, 383.54) * mm, "end": v(-10.56, 383.54) * mm});
            skLineSegment(sketch, "E66.direction1", {"start": v(-61.56, 198.12) * mm, "end": v(-36.16, 198.12) * mm, "construction": true});
            skLineSegment(sketch, "E66.direction2", {"start": v(-61.56, 198.12) * mm, "end": v(-61.56, 236.22) * mm, "construction": true});
            skSolve(sketch);
        }
        {
            var Q0;
            Q0 = qSketchRegion(id + "F34", true);
            extrude(context, id + "F35", {"entities" : qUnion([Q0]), "operationType" : NewBodyOperationType.ADD, "endBound" : BoundingType.SYMMETRIC, "depth" : 57.15 * mm});
        }
        {
            var Q0;
            Q0=makeQuery(id+"F33.opExtrude","CAP_FACE",FACE,{"disambiguationData":[OSD([sQuery(id+"F32.wireOp",EDGE,"E49")])],"isStart":false});
            var sketch = newSketch(context, id + "F36", { "sketchPlane" : qUnion([Q0])});
            skCircle(sketch, "E67", {"center": v(0, 0) * mm, "radius": 22.23 * mm});
            skCircle(sketch, "E68", {"center": v(0, 0) * mm, "radius": 88.9 * mm});
            skSolve(sketch);
        }
        {
            var Q0;
            Q0=makeQuery(id+"F36.imprint","IMPRINT",FACE,{"disambiguationData":[TD([[makeQuery(id+"F36.imprint","IMPRINT",EDGE,{"derivedFrom":sQuery(id+"F36.wireOp",EDGE,"E67")}),-1.0]])]});
            extrude(context, id + "F37", {"entities" : qUnion([Q0]), "operationType" : NewBodyOperationType.REMOVE, "oppositeDirection" : true, "depth" : 228.6 * mm});
        }
        {
            var Q0;
            Q0=makeQuery(id+"F31.opExtrude","CAP_EDGE",EDGE,{"disambiguationData":[OSD([sQuery(id+"F30.wireOp",EDGE,"E48")])],"isStart":false});
            chamfer(context, id + "F38", {"entities" : qUnion([Q0]), "chamferType" : ChamferType.TWO_OFFSETS, "width1" : 3.8 * mm, "oppositeDirection" : false, "width2" : 25.4 * mm, "tangentPropagation" : true});
        }
        {
            var Q0;
            Q0=qCreatedBy(makeId("Front.planeOp"),FACE);
            var sketch = newSketch(context, id + "F39", { "sketchPlane" : qUnion([Q0])});
            skLineSegment(sketch, "E69.0", {"start": v(-21.59, 174) * mm, "end": v(21.59, 174) * mm});
            skLineSegment(sketch, "E69.1", {"start": v(39.37, 148.6) * mm, "end": v(-39.37, 148.6) * mm});
            skLineSegment(sketch, "E70", {"start": v(21.59, 174) * mm, "end": v(23.26, 162.56) * mm});
            skLineSegment(sketch, "E71", {"start": v(23.44, 161.29) * mm, "end": v(1.63, 161.29) * mm, "construction": true});
            skLineSegment(sketch, "E72", {"start": v(23.63, 160.02) * mm, "end": v(20.9, 160.02) * mm});
            skLineSegment(sketch, "E73", {"start": v(20.9, 160.02) * mm, "end": v(20.9, 162.56) * mm});
            skLineSegment(sketch, "E74", {"start": v(20.9, 162.56) * mm, "end": v(23.26, 162.56) * mm});
            skLineSegment(sketch, "E75", {"start": v(0, 174) * mm, "end": v(0, 189.3) * mm});
            skLineSegment(sketch, "E76", {"start": v(0, 189.3) * mm, "end": v(0, 148.6) * mm});
            skLineSegment(sketch, "E77", {"start": v(23.63, 160.02) * mm, "end": v(29.75, 160.02) * mm});
            skLineSegment(sketch, "E78", {"start": v(29.75, 160.02) * mm, "end": v(30.8, 162.98) * mm});
            skLineSegment(sketch, "E79", {"start": v(30.8, 162.98) * mm, "end": v(23.26, 162.56) * mm});
            skPoint(sketch, "E80.trimOffspring.end.orphan", {"position": v(25.3, 148.6) * mm});
            skSolve(sketch);
        }
        {
            var Q0;
            Q0 = qSketchRegion(id + "F39", true);
            var Q1;
            Q1=sQuery(id+"F39.wireOp",EDGE,"E75");
            revolve(context, id + "F40", {"operationType" : NewBodyOperationType.REMOVE, "entities" : qUnion([Q0]), "axis" : qUnion([Q1]), "revolveType" : RevolveType.FULL, "oppositeDirection" : true});
        }
        {
            var Q0;
            Q0=qCreatedBy(makeId("Front.planeOp"),FACE);
            var sketch = newSketch(context, id + "F41", { "sketchPlane" : qUnion([Q0])});
            skLineSegment(sketch, "E81.0", {"start": v(-22.23, 402.6) * mm, "end": v(22.22, 402.6) * mm});
            skLineSegment(sketch, "E81.1", {"start": v(-22.23, 453.39) * mm, "end": v(22.22, 453.39) * mm});
            skLineSegment(sketch, "E82", {"start": v(22.22, 402.6) * mm, "end": v(26.59, 438.25) * mm});
            skArc(sketch, "E83", {"start": v(26.59, 438.25) * mm, "mid": v(14.87, 448.6) * mm, "end": v(0, 453.39) * mm});
            skLineSegment(sketch, "E84", {"start": v(0, 453.39) * mm, "end": v(0, 402.6) * mm});
            skLineSegment(sketch, "E85", {"start": v(26.59, 438.25) * mm, "end": v(27.56, 446.23) * mm});
            skArc(sketch, "E86", {"start": v(27.56, 446.23) * mm, "mid": v(14.14, 451.17) * mm, "end": v(0, 453.39) * mm});
            skSolve(sketch);
        }
        {
            var Q0;
            {var subQ1=sQuery(id+"F41.wireOp",EDGE,"E82");Q0=makeQuery(id+"F41.imprint","IMPRINT",FACE,{"disambiguationData":[TD([[makeQuery(id+"F41.imprint","IMPRINT",EDGE,{"derivedFrom":subQ1}),1.0]])]});}
            var Q1;
            Q1=makeQuery(id+"F41.imprint","IMPRINT",FACE,{"disambiguationData":[TD([[makeQuery(id+"F41.imprint","IMPRINT",EDGE,{"derivedFrom":sQuery(id+"F41.wireOp",EDGE,"E83")}),-1.0]])]});
            var Q2;
            Q2=sQuery(id+"F41.wireOp",EDGE,"E84");
            revolve(context, id + "F42", {"operationType" : NewBodyOperationType.ADD, "entities" : qUnion([Q0, Q1]), "axis" : qUnion([Q2]), "revolveType" : RevolveType.FULL});
        }
        {
            var Q0;
            Q0=makeQuery(id+"F42.opRevolve","SWEPT_EDGE",EDGE,{"disambiguationData":[OSD([sQuery(id+"F41.wireOp",EDGE,"E85"),sQuery(id+"F41.wireOp",EDGE,"E86")])]});
            chamfer(context, id + "F43", {"entities" : qUnion([Q0]), "width" : 5.08 * mm, "tangentPropagation" : true});
        }
        {
            var Q0;
            Q0=qCreatedBy(makeId("Front.planeOp"),FACE);
            var sketch = newSketch(context, id + "F44", { "sketchPlane" : qUnion([Q0])});
            skLineSegment(sketch, "E87", {"start": v(0, 434.6) * mm, "end": v(0, 362.58) * mm, "construction": true});
            skLineSegment(sketch, "E88.bottom", {"start": v(15.87, 428) * mm, "end": v(-15.88, 428) * mm});
            skLineSegment(sketch, "E88.top", {"start": v(15.87, 434.34) * mm, "end": v(-15.88, 434.34) * mm});
            skLineSegment(sketch, "E88.left", {"start": v(15.87, 428) * mm, "end": v(15.87, 434.34) * mm});
            skLineSegment(sketch, "E88.right", {"start": v(-15.88, 428) * mm, "end": v(-15.88, 434.34) * mm});
            skSolve(sketch);
        }
        {
            var Q0;
            Q0 = qSketchRegion(id + "F44", true);
            extrude(context, id + "F45", {"entities" : qUnion([Q0]), "operationType" : NewBodyOperationType.REMOVE, "endBound" : BoundingType.SYMMETRIC, "oppositeDirection" : true, "depth" : 76.2 * mm});
        }
        {
            var Q0;
            Q0=makeQuery(id+"F37.boolean.opBoolean","INTERSECT",EDGE,{"derivedFrom":[makeQuery(id+"F35.opExtrude","SWEPT_FACE",FACE,{"disambiguationData":[OSD([sQuery(id+"F34.wireOp",EDGE,"E50")])]}),makeQuery(id+"F37.opExtrude","SWEPT_FACE",FACE,{"disambiguationData":[OSD([sQuery(id+"F36.wireOp",EDGE,"E67")])]})]});
            var Q1;
            Q1=makeQuery(id+"F37.boolean.opBoolean","INTERSECT",EDGE,{"derivedFrom":[makeQuery(id+"F35.opExtrude","SWEPT_FACE",FACE,{"disambiguationData":[OSD([sQuery(id+"F34.wireOp",EDGE,"E51")])]}),makeQuery(id+"F37.opExtrude","SWEPT_FACE",FACE,{"disambiguationData":[OSD([sQuery(id+"F36.wireOp",EDGE,"E67")])]})]});
            var Q2;
            Q2=makeQuery(id+"F37.boolean.opBoolean","INTERSECT",EDGE,{"derivedFrom":[makeQuery(id+"F35.opExtrude","SWEPT_FACE",FACE,{"disambiguationData":[OSD([sQuery(id+"F34.wireOp",EDGE,"E66.0.1.0")])]}),makeQuery(id+"F37.opExtrude","SWEPT_FACE",FACE,{"disambiguationData":[OSD([sQuery(id+"F36.wireOp",EDGE,"E67")])]})]});
            var Q3;
            Q3=makeQuery(id+"F37.boolean.opBoolean","INTERSECT",EDGE,{"derivedFrom":[makeQuery(id+"F35.opExtrude","SWEPT_FACE",FACE,{"disambiguationData":[OSD([sQuery(id+"F34.wireOp",EDGE,"E66.0.1.16")])]}),makeQuery(id+"F37.opExtrude","SWEPT_FACE",FACE,{"disambiguationData":[OSD([sQuery(id+"F36.wireOp",EDGE,"E67")])]})]});
            var Q4;
            {var subQ0=sQuery(id+"F30.wireOp",EDGE,"E48");Q4=makeQuery(id+"F38.opChamfer","BLEND_EDGE",EDGE,{"blendedFrom":[makeQuery(id+"F31.opExtrude","CAP_EDGE",EDGE,{"disambiguationData":[OSD([subQ0])],"isStart":false}),makeQuery(id+"F31.opExtrude","CAP_FACE",FACE,{"disambiguationData":[OSD([subQ0])],"isStart":false})],"blendedInto":[makeQuery(id+"F31.opExtrude","CAP_FACE",FACE,{"disambiguationData":[OSD([subQ0])],"isStart":false})]});}
            var Q5;
            Q5=makeQuery(id+"F37.boolean.opBoolean","INTERSECT",EDGE,{"derivedFrom":[makeQuery(id+"F35.opExtrude","SWEPT_FACE",FACE,{"disambiguationData":[OSD([sQuery(id+"F34.wireOp",EDGE,"E66.0.2.12")])]}),makeQuery(id+"F37.opExtrude","SWEPT_FACE",FACE,{"disambiguationData":[OSD([sQuery(id+"F36.wireOp",EDGE,"E67")])]})]});
            var Q6;
            Q6=makeQuery(id+"F37.boolean.opBoolean","INTERSECT",EDGE,{"derivedFrom":[makeQuery(id+"F35.opExtrude","SWEPT_FACE",FACE,{"disambiguationData":[OSD([sQuery(id+"F34.wireOp",EDGE,"E66.0.2.13")])]}),makeQuery(id+"F37.opExtrude","SWEPT_FACE",FACE,{"disambiguationData":[OSD([sQuery(id+"F36.wireOp",EDGE,"E67")])]})]});
            var Q7;
            Q7=makeQuery(id+"F37.boolean.opBoolean","INTERSECT",EDGE,{"derivedFrom":[makeQuery(id+"F35.opExtrude","SWEPT_FACE",FACE,{"disambiguationData":[OSD([sQuery(id+"F34.wireOp",EDGE,"E66.0.3.12")])]}),makeQuery(id+"F37.opExtrude","SWEPT_FACE",FACE,{"disambiguationData":[OSD([sQuery(id+"F36.wireOp",EDGE,"E67")])]})]});
            var Q8;
            Q8=makeQuery(id+"F37.boolean.opBoolean","INTERSECT",EDGE,{"derivedFrom":[makeQuery(id+"F35.opExtrude","SWEPT_FACE",FACE,{"disambiguationData":[OSD([sQuery(id+"F34.wireOp",EDGE,"E66.0.3.13")])]}),makeQuery(id+"F37.opExtrude","SWEPT_FACE",FACE,{"disambiguationData":[OSD([sQuery(id+"F36.wireOp",EDGE,"E67")])]})]});
            var Q9;
            Q9=makeQuery(id+"F37.boolean.opBoolean","INTERSECT",EDGE,{"derivedFrom":[makeQuery(id+"F35.opExtrude","SWEPT_FACE",FACE,{"disambiguationData":[OSD([sQuery(id+"F34.wireOp",EDGE,"E66.0.4.12")])]}),makeQuery(id+"F37.opExtrude","SWEPT_FACE",FACE,{"disambiguationData":[OSD([sQuery(id+"F36.wireOp",EDGE,"E67")])]})]});
            var Q10;
            Q10=makeQuery(id+"F37.boolean.opBoolean","INTERSECT",EDGE,{"derivedFrom":[makeQuery(id+"F35.opExtrude","SWEPT_FACE",FACE,{"disambiguationData":[OSD([sQuery(id+"F34.wireOp",EDGE,"E66.0.4.13")])]}),makeQuery(id+"F37.opExtrude","SWEPT_FACE",FACE,{"disambiguationData":[OSD([sQuery(id+"F36.wireOp",EDGE,"E67")])]})]});
            var Q11;
            Q11=makeQuery(id+"F37.boolean.opBoolean","INTERSECT",EDGE,{"derivedFrom":[makeQuery(id+"F35.opExtrude","SWEPT_FACE",FACE,{"disambiguationData":[OSD([sQuery(id+"F34.wireOp",EDGE,"E66.0.5.12")])]}),makeQuery(id+"F37.opExtrude","SWEPT_FACE",FACE,{"disambiguationData":[OSD([sQuery(id+"F36.wireOp",EDGE,"E67")])]})]});
            var Q12;
            Q12=makeQuery(id+"F37.boolean.opBoolean","INTERSECT",EDGE,{"derivedFrom":[makeQuery(id+"F35.opExtrude","SWEPT_FACE",FACE,{"disambiguationData":[OSD([sQuery(id+"F34.wireOp",EDGE,"E66.0.5.13")])]}),makeQuery(id+"F37.opExtrude","SWEPT_FACE",FACE,{"disambiguationData":[OSD([sQuery(id+"F36.wireOp",EDGE,"E67")])]})]});
            var Q13;
            Q13=makeQuery(id+"F33.opExtrude","CAP_EDGE",EDGE,{"disambiguationData":[OSD([sQuery(id+"F32.wireOp",EDGE,"E49")])],"isStart":false});
            var Q14;
            Q14=makeQuery(id+"F42.opRevolve","SWEPT_EDGE",EDGE,{"disambiguationData":[OSD([sQuery(id+"F41.wireOp",EDGE,"E81.0"),sQuery(id+"F41.wireOp",EDGE,"E82")])]});
            chamfer(context, id + "F46", {"entities" : qUnion([Q0, Q1, Q2, Q3, Q4, Q5, Q6, Q7, Q8, Q9, Q10, Q11, Q12, Q13, Q14]), "width" : 1.27 * mm, "tangentPropagation" : true});
        }
        {
            var Q0;
            Q0=makeQuery(id+"F38.opChamfer","BLEND_EDGE",EDGE,{"blendedFrom":[makeQuery(id+"F31.opExtrude","CAP_EDGE",EDGE,{"disambiguationData":[OSD([sQuery(id+"F30.wireOp",EDGE,"E48")])],"isStart":false}),makeQuery(id+"F13.boolean.opBoolean","COPY",FACE,{"derivedFrom":makeQuery(id+"F13.opExtrude","SWEPT_FACE",FACE,{"disambiguationData":[OSD([sQuery(id+"F12.wireOp",EDGE,"E4"),sQuery(id+"F12.wireOp",EDGE,"E6.0.MirrorCS")])]})})],"blendedInto":[makeQuery(id+"F13.boolean.opBoolean","COPY",FACE,{"derivedFrom":makeQuery(id+"F13.opExtrude","SWEPT_FACE",FACE,{"disambiguationData":[OSD([sQuery(id+"F12.wireOp",EDGE,"E4"),sQuery(id+"F12.wireOp",EDGE,"E6.0.MirrorCS")])]})})]});
            fillet(context, id + "F47", {"entities" : qUnion([Q0]), "radius" : 1.27 * mm, "tangentPropagation" : true, "allowEdgeOverflow" : false});
        }
    });
